# Revit family: IS_Connect_T9806_BIM_FR
name_source: partatom
category: Plumbing Fixtures
revit_build: Autodesk Revit 2017 (Build: 20160225_1515(x64)
units: mm (PartAtom-declared; Revit-internal decimal feet)

## family parameters
Cut with Voids When Loaded = No
Host = Face
OmniClass Number = 23.45.05.14.17.11
OmniClass Title = Shower Compartments
Part Type = Normal
Room Calculation Point = No
Round Connector Dimension = Use Diameter
Shared = No

## types (1)
- T9806EO - CONNECT SPRCHOVY KOUT ČTVEREC 90 CM
    Accessoires = www.idealstandard.be
    Assembly Code = C1030200
    Bim-NomDuProjet = ISI_IdealStandard_Connect_T9806
    Caractéristiques = Porte 90 cmverre Transparent
    ConseilsDInstallation = www.idealstandard.be
    Cost = 0 $
    CoûtDeRemplacement = 0
    DateDeCréation = 2018_08_15
    Default Elevation = 0 mm  [stored 0 ft]
    Description = Porte 90 cmverre Transparent
    Dimensions = 0 x 0 x 0 mm
    Espace = Interne
    Forme = Complexe
    Hauteur = 0 mm  [stored 0 ft]
    InformationsProduit = www.idealstandard.be
    Largeur = 0 mm  [stored 0 ft]
    LienUtile = www.idealstandard.be
    Longueur = 0 mm  [stored 0 ft]
    Manufacturer = www.idealstandard.be
    Marque = Ideal Standard
    Model = T9806EO
    PoidsNet = 0
    Profondeur = 0 mm  [stored 0 ft]
    Raccordement = Plomberie
    Révision = 1
    URL = www.idealstandard.be
    UnitéDeMesure = Millimètres
    UnitéDeTemps = An
    UnitéMonétaire = €
    UrlDuFabricant = www.idealstandard.be

note: [stored X ft] marks values corroborated as IEEE doubles in the binary element streams (Revit-internal decimal feet)

## geometry (parser evidence)
native form markers: Sweep x1
no freeform markers — native parametric forms only
